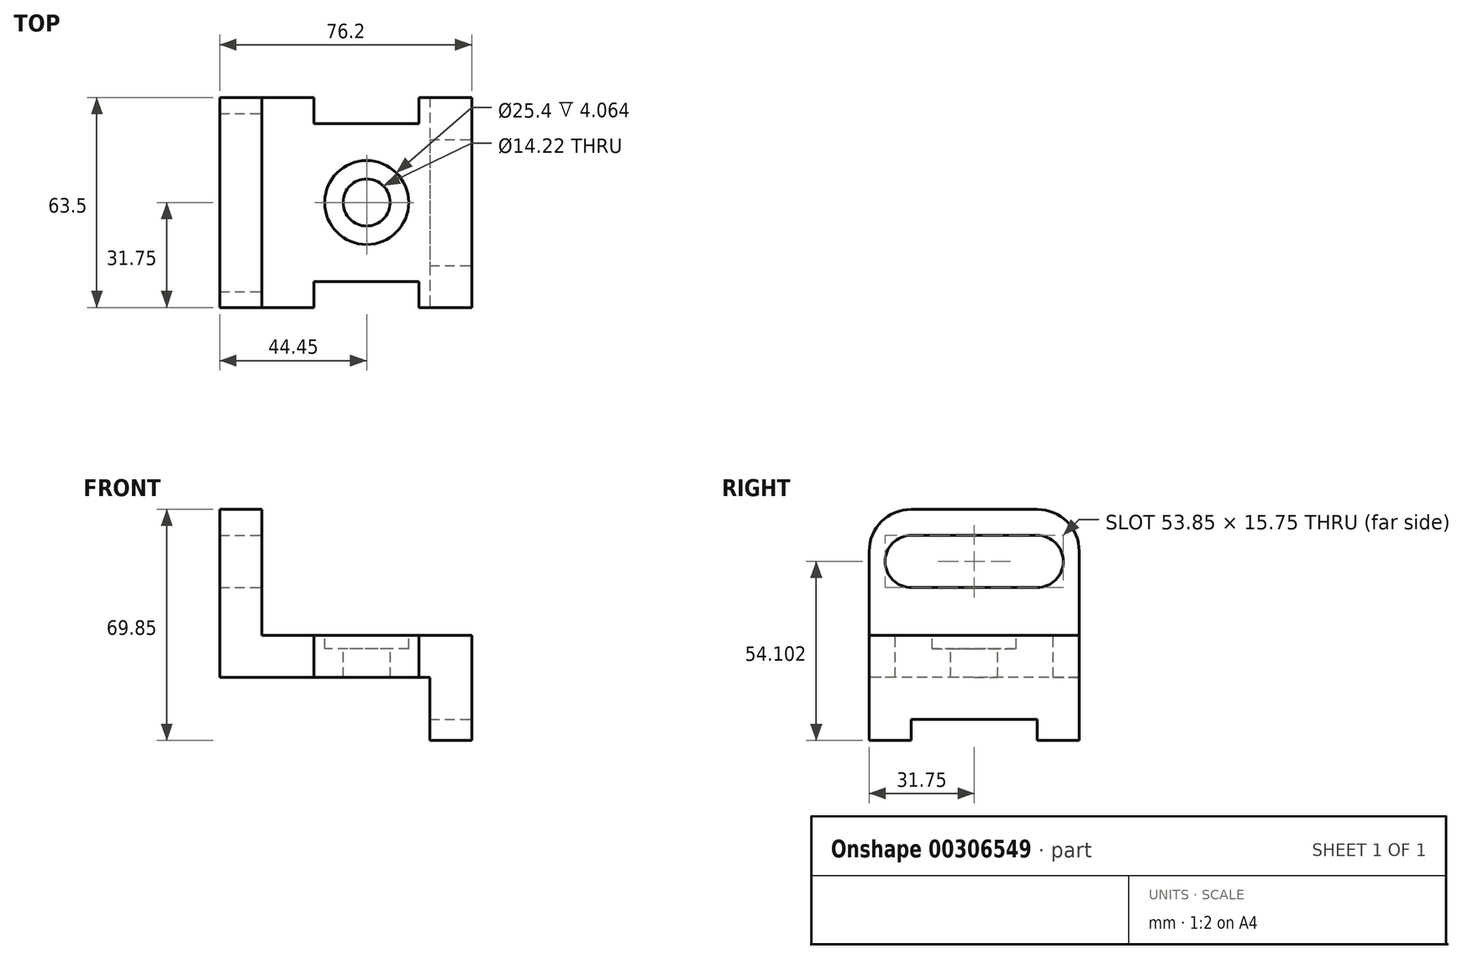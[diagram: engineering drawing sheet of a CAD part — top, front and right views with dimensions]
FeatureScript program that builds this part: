
annotation { "Feature Type Name" : "Feature", "Feature Type Description" : "" }
export const myFeature = defineFeature(function(context is Context, id is Id, definition is map)
    precondition{}
    {
        {
            var Q0;
            Q0=qCreatedBy(makeId("Front.planeOp"),FACE);
            var sketch = newSketch(context, id + "F0", { "sketchPlane" : qUnion([Q0])});
            skLineSegment(sketch, "E0.bottom", {"start": v(0, 0) * mm, "end": v(76.2, 0) * mm});
            skLineSegment(sketch, "E0.top", {"start": v(0, 69.85) * mm, "end": v(76.2, 69.85) * mm});
            skLineSegment(sketch, "E0.left", {"start": v(0, 0) * mm, "end": v(0, 69.85) * mm});
            skLineSegment(sketch, "E0.right", {"start": v(76.2, 0) * mm, "end": v(76.2, 69.85) * mm});
            skSolve(sketch);
        }
        {
            var Q0;
            Q0=makeQuery(id+"F0.imprint","IMPRINT",FACE,{"disambiguationData":[TD([[makeQuery(id+"F0.imprint","IMPRINT",EDGE,{"derivedFrom":sQuery(id+"F0.wireOp",EDGE,"E0.bottom")}),1.0]])]});
            extrude(context, id + "F1", {"entities" : qUnion([Q0]), "depth" : 63.5 * mm});
        }
        {
            var Q0;
            Q0=makeQuery(id+"F1.opExtrude","SWEPT_FACE",FACE,{"disambiguationData":[OSD([sQuery(id+"F0.wireOp",EDGE,"E0.right")])]});
            var sketch = newSketch(context, id + "F2", { "sketchPlane" : qUnion([Q0])});
            skLineSegment(sketch, "E1.bottom", {"start": v(-50.8, 0) * mm, "end": v(-12.7, 0) * mm});
            skLineSegment(sketch, "E1.top", {"start": v(-50.8, 6.35) * mm, "end": v(-12.7, 6.35) * mm});
            skLineSegment(sketch, "E1.left", {"start": v(-50.8, 0) * mm, "end": v(-50.8, 6.35) * mm});
            skLineSegment(sketch, "E1.right", {"start": v(-12.7, 0) * mm, "end": v(-12.7, 6.35) * mm});
            skSolve(sketch);
        }
        {
            var Q0;
            Q0 = qSketchRegion(id + "F2", true);
            extrude(context, id + "F3", {"entities" : qUnion([Q0]), "operationType" : NewBodyOperationType.REMOVE, "endBound" : BoundingType.THROUGH_ALL, "oppositeDirection" : true, "depth" : 25.4 * mm});
        }
        {
            var Q0;
            Q0=makeQuery(id+"F1.opExtrude","CAP_FACE",FACE,{"disambiguationData":[OSD([sQuery(id+"F0.wireOp",EDGE,"E0.bottom"),sQuery(id+"F0.wireOp",EDGE,"E0.top"),sQuery(id+"F0.wireOp",EDGE,"E0.left"),sQuery(id+"F0.wireOp",EDGE,"E0.right")])],"isStart":false});
            var sketch = newSketch(context, id + "F4", { "sketchPlane" : qUnion([Q0])});
            skLineSegment(sketch, "E2.bottom", {"start": v(0, 0) * mm, "end": v(63.5, 0) * mm});
            skLineSegment(sketch, "E2.top", {"start": v(0, 19.05) * mm, "end": v(63.5, 19.05) * mm});
            skLineSegment(sketch, "E2.left", {"start": v(0, 0) * mm, "end": v(0, 19.05) * mm});
            skLineSegment(sketch, "E2.right", {"start": v(63.5, 0) * mm, "end": v(63.5, 19.05) * mm});
            skSolve(sketch);
        }
        {
            var Q0;
            Q0 = qSketchRegion(id + "F4", true);
            extrude(context, id + "F5", {"entities" : qUnion([Q0]), "operationType" : NewBodyOperationType.REMOVE, "endBound" : BoundingType.THROUGH_ALL, "oppositeDirection" : true, "depth" : 25.4 * mm});
        }
        {
            var Q0;
            Q0=makeQuery(id+"F1.opExtrude","CAP_FACE",FACE,{"disambiguationData":[OSD([sQuery(id+"F0.wireOp",EDGE,"E0.bottom"),sQuery(id+"F0.wireOp",EDGE,"E0.top"),sQuery(id+"F0.wireOp",EDGE,"E0.left"),sQuery(id+"F0.wireOp",EDGE,"E0.right")])],"isStart":false});
            var sketch = newSketch(context, id + "F6", { "sketchPlane" : qUnion([Q0])});
            skLineSegment(sketch, "E3.bottom", {"start": v(12.7, 69.85) * mm, "end": v(76.2, 69.85) * mm});
            skLineSegment(sketch, "E3.top", {"start": v(12.7, 31.75) * mm, "end": v(76.2, 31.75) * mm});
            skLineSegment(sketch, "E3.left", {"start": v(12.7, 69.85) * mm, "end": v(12.7, 31.75) * mm});
            skLineSegment(sketch, "E3.right", {"start": v(76.2, 69.85) * mm, "end": v(76.2, 31.75) * mm});
            skSolve(sketch);
        }
        {
            var Q0;
            Q0 = qSketchRegion(id + "F6", true);
            extrude(context, id + "F7", {"entities" : qUnion([Q0]), "operationType" : NewBodyOperationType.REMOVE, "endBound" : BoundingType.THROUGH_ALL, "oppositeDirection" : true, "depth" : 25.4 * mm});
        }
        {
            var Q0;
            Q0=makeQuery(id+"F7.boolean.opBoolean","COPY",FACE,{"derivedFrom":makeQuery(id+"F7.opExtrude","SWEPT_FACE",FACE,{"disambiguationData":[OSD([sQuery(id+"F6.wireOp",EDGE,"E3.top")])]})});
            var sketch = newSketch(context, id + "F8", { "sketchPlane" : qUnion([Q0])});
            skLineSegment(sketch, "E4.bottom", {"start": v(28.45, -63.5) * mm, "end": v(60.2, -63.5) * mm});
            skLineSegment(sketch, "E4.top", {"start": v(28.45, -55.63) * mm, "end": v(60.2, -55.63) * mm});
            skLineSegment(sketch, "E4.left", {"start": v(28.45, -63.5) * mm, "end": v(28.45, -55.63) * mm});
            skLineSegment(sketch, "E4.right", {"start": v(60.2, -63.5) * mm, "end": v(60.2, -55.63) * mm});
            skLineSegment(sketch, "E5.bottom", {"start": v(28.45, 0) * mm, "end": v(60.2, 0) * mm});
            skLineSegment(sketch, "E5.top", {"start": v(28.45, -7.87) * mm, "end": v(60.2, -7.87) * mm});
            skLineSegment(sketch, "E5.left", {"start": v(28.45, 0) * mm, "end": v(28.45, -7.87) * mm});
            skLineSegment(sketch, "E5.right", {"start": v(60.2, 0) * mm, "end": v(60.2, -7.87) * mm});
            skSolve(sketch);
        }
        {
            var Q0;
            Q0 = qSketchRegion(id + "F8", true);
            extrude(context, id + "F9", {"entities" : qUnion([Q0]), "operationType" : NewBodyOperationType.REMOVE, "oppositeDirection" : true, "depth" : 25.4 * mm});
        }
        {
            var Q0;
            Q0=makeQuery(id+"F7.boolean.opBoolean","COPY",FACE,{"derivedFrom":makeQuery(id+"F7.opExtrude","SWEPT_FACE",FACE,{"disambiguationData":[OSD([sQuery(id+"F6.wireOp",EDGE,"E3.left")])]})});
            var sketch = newSketch(context, id + "F10", { "sketchPlane" : qUnion([Q0])});
            skLineSegment(sketch, "E6.bottom", {"start": v(-50.8, 69.85) * mm, "end": v(-12.7, 69.85) * mm});
            skLineSegment(sketch, "E6.top", {"start": v(-63.5, 31.75) * mm, "end": v(0, 31.75) * mm});
            skLineSegment(sketch, "E6.left", {"start": v(-63.5, 57.15) * mm, "end": v(-63.5, 31.75) * mm});
            skLineSegment(sketch, "E6.right", {"start": v(0, 57.15) * mm, "end": v(0, 31.75) * mm});
            skPoint(sketch, "E7.visualSharp", {"position": v(-63.5, 69.85) * mm});
            skArc(sketch, "E7.filletArc", {"start": v(-50.8, 69.85) * mm, "mid": v(-59.78, 66.13) * mm, "end": v(-63.5, 57.15) * mm});
            skPoint(sketch, "E8.visualSharp", {"position": v(0, 69.85) * mm});
            skArc(sketch, "E8.filletArc", {"start": v(0, 57.15) * mm, "mid": v(-3.72, 66.13) * mm, "end": v(-12.7, 69.85) * mm});
            skLineSegment(sketch, "E9", {"start": v(-63.5, 57.15) * mm, "end": v(-63.5, 69.85) * mm});
            skLineSegment(sketch, "E10", {"start": v(-12.7, 69.85) * mm, "end": v(0, 69.85) * mm});
            skSolve(sketch);
        }
        {
            var Q0;
            {var subQ0=sQuery(id+"F10.wireOp",EDGE,"E7.filletArc");Q0=makeQuery(id+"F10.imprint","IMPRINT",FACE,{"disambiguationData":[TD([[makeQuery(id+"F10.imprint","IMPRINT",EDGE,{"derivedFrom":subQ0}),-1.0]])]});}
            var Q1;
            {var subQ0=sQuery(id+"F10.wireOp",EDGE,"E8.filletArc");Q1=makeQuery(id+"F10.imprint","IMPRINT",FACE,{"disambiguationData":[TD([[makeQuery(id+"F10.imprint","IMPRINT",EDGE,{"derivedFrom":subQ0}),-1.0]])]});}
            extrude(context, id + "F11", {"entities" : qUnion([Q0, Q1]), "operationType" : NewBodyOperationType.REMOVE, "oppositeDirection" : true, "depth" : 25.4 * mm});
        }
        {
            var Q0;
            Q0=makeQuery(id+"F7.boolean.opBoolean","COPY",FACE,{"derivedFrom":makeQuery(id+"F7.opExtrude","SWEPT_FACE",FACE,{"disambiguationData":[OSD([sQuery(id+"F6.wireOp",EDGE,"E3.left")])]})});
            var sketch = newSketch(context, id + "F12", { "sketchPlane" : qUnion([Q0])});
            skLineSegment(sketch, "E11.bottom", {"start": v(-50.8, 61.98) * mm, "end": v(-12.7, 61.98) * mm});
            skLineSegment(sketch, "E11.top", {"start": v(-50.8, 46.23) * mm, "end": v(-12.7, 46.23) * mm});
            skLineSegment(sketch, "E11.left", {"start": v(-50.8, 61.98) * mm, "end": v(-50.8, 46.23) * mm});
            skLineSegment(sketch, "E11.right", {"start": v(-12.7, 61.98) * mm, "end": v(-12.7, 46.23) * mm});
            skArc(sketch, "E12", {"start": v(-50.8, 61.98) * mm, "mid": v(-58.67, 54.1) * mm, "end": v(-50.8, 46.23) * mm});
            skArc(sketch, "E13", {"start": v(-12.7, 46.23) * mm, "mid": v(-4.83, 54.1) * mm, "end": v(-12.7, 61.98) * mm});
            skSolve(sketch);
        }
        {
            var Q0;
            Q0 = qSketchRegion(id + "F12", true);
            extrude(context, id + "F13", {"entities" : qUnion([Q0]), "operationType" : NewBodyOperationType.REMOVE, "endBound" : BoundingType.THROUGH_ALL, "oppositeDirection" : true, "depth" : 25.4 * mm});
        }
        {
            var Q0;
            Q0=makeQuery(id+"F7.boolean.opBoolean","COPY",FACE,{"derivedFrom":makeQuery(id+"F7.opExtrude","SWEPT_FACE",FACE,{"disambiguationData":[OSD([sQuery(id+"F6.wireOp",EDGE,"E3.top")])]})});
            var sketch = newSketch(context, id + "F14", { "sketchPlane" : qUnion([Q0])});
            skCircle(sketch, "E14", {"center": v(44.45, -31.75) * mm, "radius": 12.7 * mm});
            skCircle(sketch, "E15", {"center": v(44.45, -31.75) * mm, "radius": 7.11 * mm});
            skSolve(sketch);
        }
        {
            var Q0;
            Q0=makeQuery(id+"F14.imprint","IMPRINT",FACE,{"disambiguationData":[TD([[makeQuery(id+"F14.imprint","IMPRINT",EDGE,{"derivedFrom":sQuery(id+"F14.wireOp",EDGE,"E14")}),1.0]])]});
            extrude(context, id + "F15", {"entities" : qUnion([Q0]), "operationType" : NewBodyOperationType.REMOVE, "oppositeDirection" : true, "depth" : 4.06 * mm});
        }
        {
            var Q0;
            Q0=makeQuery(id+"F15.boolean.opBoolean","SPLIT",FACE,{"disambiguationData":[TD([makeQuery(id+"F15.opExtrude","SWEPT_FACE",FACE,{"disambiguationData":[OSD([sQuery(id+"F14.wireOp",EDGE,"E15")])]})])],"derivedFrom":makeQuery(id+"F7.boolean.opBoolean","COPY",FACE,{"derivedFrom":makeQuery(id+"F7.opExtrude","SWEPT_FACE",FACE,{"disambiguationData":[OSD([sQuery(id+"F6.wireOp",EDGE,"E3.top")])]})})});
            extrude(context, id + "F16", {"entities" : qUnion([Q0]), "operationType" : NewBodyOperationType.REMOVE, "endBound" : BoundingType.THROUGH_ALL, "oppositeDirection" : true, "depth" : 25.4 * mm});
        }
    });
